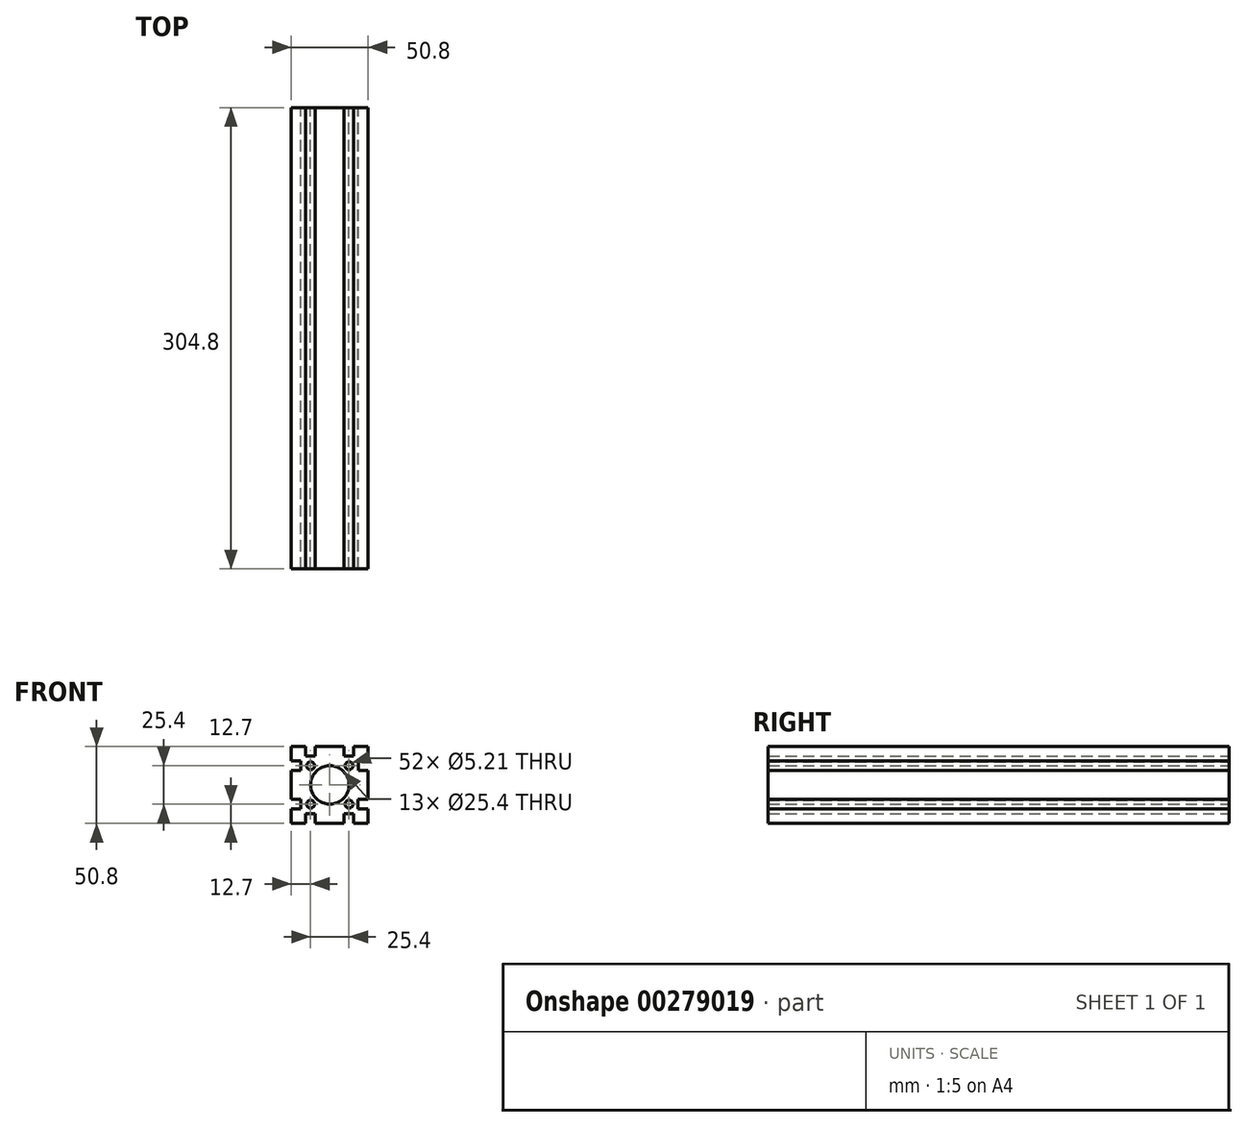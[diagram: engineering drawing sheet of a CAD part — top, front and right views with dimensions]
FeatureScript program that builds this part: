
annotation { "Feature Type Name" : "Feature", "Feature Type Description" : "" }
export const myFeature = defineFeature(function(context is Context, id is Id, definition is map)
    precondition{}
    {
        {
            var Q0;
            Q0=qCreatedBy(makeId("Front.planeOp"),FACE);
            var sketch = newSketch(context, id + "F0", { "sketchPlane" : qUnion([Q0])});
            skLineSegment(sketch, "E0.bottom", {"start": v(25.4, -25.4) * mm, "end": v(15.88, -25.4) * mm});
            skLineSegment(sketch, "E0.top", {"start": v(25.4, 25.4) * mm, "end": v(15.87, 25.4) * mm});
            skLineSegment(sketch, "E0.left", {"start": v(25.4, -25.4) * mm, "end": v(25.4, -15.88) * mm});
            skLineSegment(sketch, "E0.right", {"start": v(-25.4, -25.4) * mm, "end": v(-25.4, -15.88) * mm});
            skPoint(sketch, "E0.middle", {"position": v(0, 0) * mm});
            skLineSegment(sketch, "E1.0", {"start": v(25.4, 12.7) * mm, "end": v(-25.4, 12.7) * mm, "construction": true});
            skLineSegment(sketch, "E2.0", {"start": v(25, -12.7) * mm, "end": v(-25.4, -12.7) * mm, "construction": true});
            skLineSegment(sketch, "E3.0", {"start": v(-12.7, -25.4) * mm, "end": v(-12.7, 25.4) * mm, "construction": true});
            skLineSegment(sketch, "E4.0", {"start": v(12.7, -25.4) * mm, "end": v(12.7, 25.4) * mm, "construction": true});
            skCircle(sketch, "E5", {"center": v(-12.7, 12.7) * mm, "radius": 2.6 * mm});
            skCircle(sketch, "E6", {"center": v(12.7, 12.7) * mm, "radius": 2.6 * mm});
            skCircle(sketch, "E7", {"center": v(-12.7, -12.7) * mm, "radius": 2.6 * mm});
            skCircle(sketch, "E8", {"center": v(12.7, -12.7) * mm, "radius": 2.6 * mm});
            skLineSegment(sketch, "E9.bottom", {"start": v(25.4, 9.53) * mm, "end": v(19.05, 9.53) * mm});
            skLineSegment(sketch, "E9.top", {"start": v(25.4, 15.88) * mm, "end": v(19.05, 15.88) * mm});
            skLineSegment(sketch, "E9.right", {"start": v(19.05, 9.53) * mm, "end": v(19.05, 15.88) * mm});
            skPoint(sketch, "E9.middle", {"position": v(25.4, 12.7) * mm});
            skLineSegment(sketch, "E10.bottom", {"start": v(9.52, 19.05) * mm, "end": v(15.87, 19.05) * mm});
            skLineSegment(sketch, "E10.left", {"start": v(9.52, 19.05) * mm, "end": v(9.52, 25.4) * mm});
            skLineSegment(sketch, "E10.right", {"start": v(15.87, 19.05) * mm, "end": v(15.87, 25.4) * mm});
            skPoint(sketch, "E10.middle", {"position": v(12.7, 25.4) * mm});
            skLineSegment(sketch, "E11.bottom", {"start": v(-9.53, 19.05) * mm, "end": v(-15.88, 19.05) * mm});
            skLineSegment(sketch, "E11.left", {"start": v(-9.53, 19.05) * mm, "end": v(-9.53, 25.4) * mm});
            skLineSegment(sketch, "E11.right", {"start": v(-15.88, 19.05) * mm, "end": v(-15.88, 25.4) * mm});
            skPoint(sketch, "E11.middle", {"position": v(-12.7, 25.4) * mm});
            skLineSegment(sketch, "E12.bottom", {"start": v(-25.4, 9.53) * mm, "end": v(-19.05, 9.53) * mm});
            skLineSegment(sketch, "E12.top", {"start": v(-25.4, 15.88) * mm, "end": v(-19.05, 15.88) * mm});
            skLineSegment(sketch, "E12.right", {"start": v(-19.05, 9.53) * mm, "end": v(-19.05, 15.88) * mm});
            skPoint(sketch, "E12.middle", {"position": v(-25.4, 12.7) * mm});
            skLineSegment(sketch, "E13.bottom", {"start": v(-25.4, -15.88) * mm, "end": v(-19.05, -15.87) * mm});
            skLineSegment(sketch, "E13.top", {"start": v(-25.4, -9.53) * mm, "end": v(-19.05, -9.52) * mm});
            skLineSegment(sketch, "E13.right", {"start": v(-19.05, -15.88) * mm, "end": v(-19.05, -9.52) * mm});
            skPoint(sketch, "E13.middle", {"position": v(-25.4, -12.7) * mm});
            skLineSegment(sketch, "E14.top", {"start": v(-9.52, -19.05) * mm, "end": v(-15.88, -19.05) * mm});
            skLineSegment(sketch, "E14.left", {"start": v(-9.52, -25.4) * mm, "end": v(-9.52, -19.05) * mm});
            skLineSegment(sketch, "E14.right", {"start": v(-15.88, -25.4) * mm, "end": v(-15.88, -19.05) * mm});
            skPoint(sketch, "E14.middle", {"position": v(-12.7, -25.4) * mm});
            skLineSegment(sketch, "E15.top", {"start": v(15.88, -19.05) * mm, "end": v(9.53, -19.05) * mm});
            skLineSegment(sketch, "E15.left", {"start": v(15.88, -25.4) * mm, "end": v(15.88, -19.05) * mm});
            skLineSegment(sketch, "E15.right", {"start": v(9.53, -25.4) * mm, "end": v(9.53, -19.05) * mm});
            skPoint(sketch, "E15.middle", {"position": v(12.7, -25.4) * mm});
            skLineSegment(sketch, "E16.bottom", {"start": v(25.4, -15.88) * mm, "end": v(18.65, -15.88) * mm});
            skLineSegment(sketch, "E16.top", {"start": v(25.4, -9.52) * mm, "end": v(18.65, -9.52) * mm});
            skLineSegment(sketch, "E16.right", {"start": v(18.65, -15.88) * mm, "end": v(18.65, -9.52) * mm});
            skPoint(sketch, "E16.middle", {"position": v(25, -12.7) * mm});
            skPoint(sketch, "E11.top.end.orphan", {"position": v(-15.88, 31.75) * mm});
            skPoint(sketch, "E11.top.start.orphan", {"position": v(-9.53, 31.75) * mm});
            skLineSegment(sketch, "E17.trimOffspring", {"start": v(-15.88, 25.4) * mm, "end": v(-25.4, 25.4) * mm});
            skPoint(sketch, "E18.orphan", {"position": v(9.52, 31.75) * mm});
            skPoint(sketch, "E19.orphan", {"position": v(15.87, 31.75) * mm});
            skLineSegment(sketch, "E20.trimOffspring", {"start": v(9.52, 25.4) * mm, "end": v(-9.53, 25.4) * mm});
            skPoint(sketch, "E9.left.end.orphan", {"position": v(31.75, 15.88) * mm});
            skPoint(sketch, "E21.orphan", {"position": v(31.75, 9.53) * mm});
            skPoint(sketch, "E12.left.start.orphan", {"position": v(-31.75, 9.53) * mm});
            skPoint(sketch, "E22.orphan", {"position": v(-31.75, 15.88) * mm});
            skLineSegment(sketch, "E23.trimOffspring", {"start": v(25.4, 15.88) * mm, "end": v(25.4, 25.4) * mm});
            skLineSegment(sketch, "E24.trimOffspring", {"start": v(-25.4, 15.88) * mm, "end": v(-25.4, 25.4) * mm});
            skPoint(sketch, "E13.left.end.orphan", {"position": v(-31.75, -9.53) * mm});
            skPoint(sketch, "E25.orphan", {"position": v(-31.75, -15.88) * mm});
            skLineSegment(sketch, "E26.trimOffspring", {"start": v(-25.4, -9.53) * mm, "end": v(-25.4, 9.53) * mm});
            skLineSegment(sketch, "E27.trimOffspring", {"start": v(-15.88, -25.4) * mm, "end": v(-25.4, -25.4) * mm});
            skPoint(sketch, "E14.bottom.end.orphan", {"position": v(-15.88, -31.75) * mm});
            skPoint(sketch, "E14.bottom.start.orphan", {"position": v(-9.52, -31.75) * mm});
            skPoint(sketch, "E15.bottom.end.orphan", {"position": v(9.53, -31.75) * mm});
            skPoint(sketch, "E28.orphan", {"position": v(15.88, -31.75) * mm});
            skLineSegment(sketch, "E29.trimOffspring", {"start": v(9.53, -25.4) * mm, "end": v(-9.53, -25.4) * mm});
            skLineSegment(sketch, "E30.trimOffspring", {"start": v(25.4, -9.52) * mm, "end": v(25.4, 9.53) * mm});
            skPoint(sketch, "E16.left.end.orphan", {"position": v(31.35, -9.52) * mm});
            skPoint(sketch, "E16.left.start.orphan", {"position": v(31.35, -15.88) * mm});
            skCircle(sketch, "E31", {"center": v(0, 0) * mm, "radius": 12.7 * mm});
            skSolve(sketch);
        }
        {
            var Q0;
            Q0=makeQuery(id+"F0.imprint","IMPRINT",FACE,{"disambiguationData":[TD([[makeQuery(id+"F0.imprint","IMPRINT",EDGE,{"derivedFrom":sQuery(id+"F0.wireOp",EDGE,"E0.bottom")}),-1.0]])]});
            extrude(context, id + "F1", {"entities" : qUnion([Q0]), "endBound" : BoundingType.SYMMETRIC, "depth" : 304.8 * mm});
        }
    });
